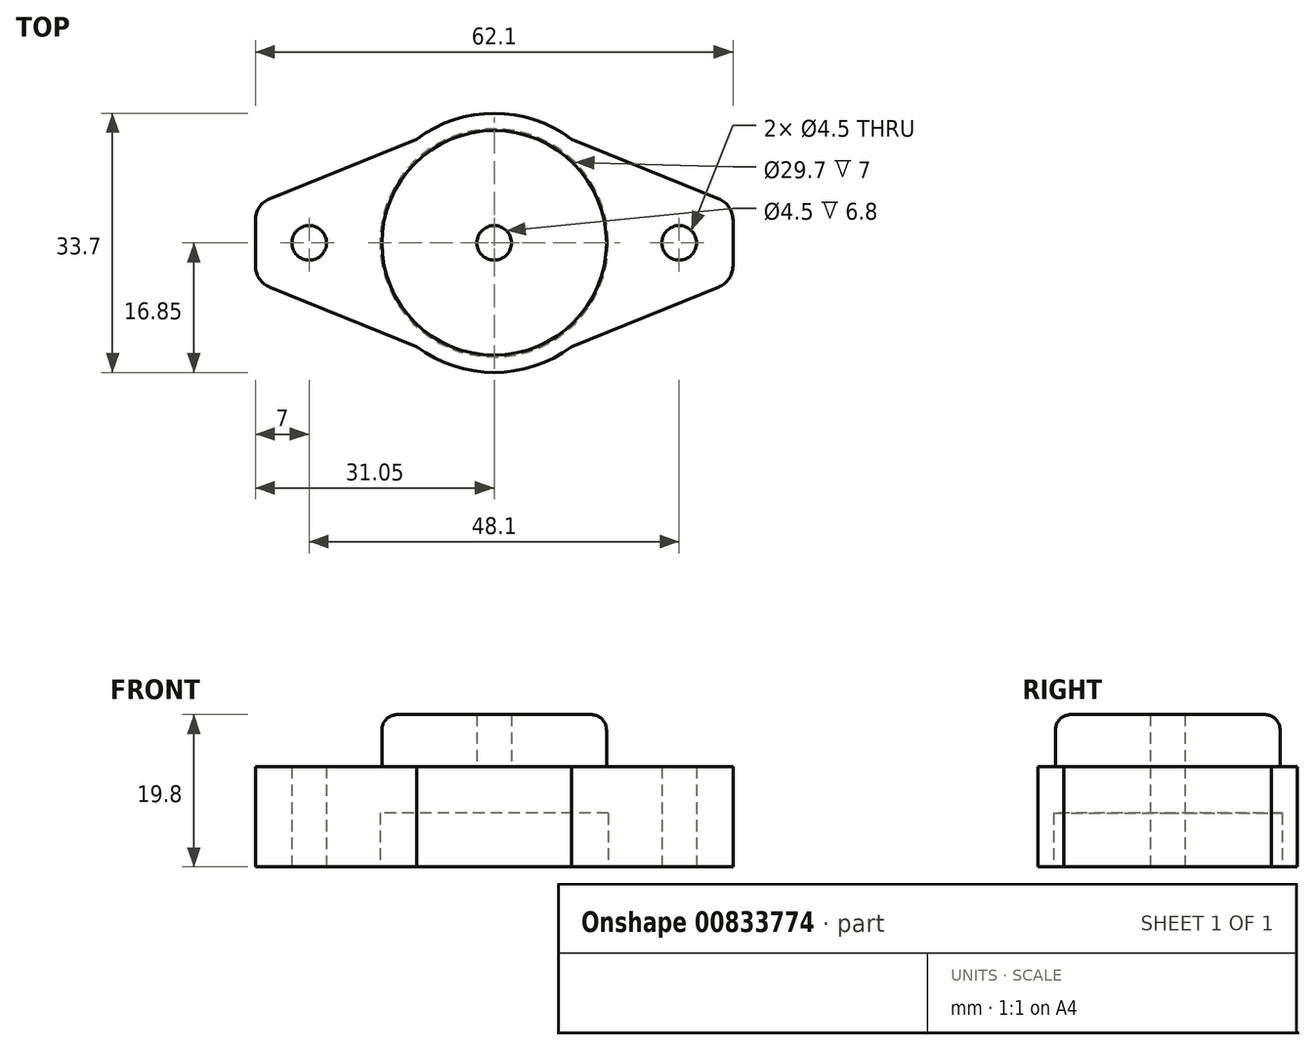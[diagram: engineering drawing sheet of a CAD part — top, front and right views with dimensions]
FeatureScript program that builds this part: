
annotation { "Feature Type Name" : "Feature", "Feature Type Description" : "" }
export const myFeature = defineFeature(function(context is Context, id is Id, definition is map)
    precondition{}
    {
        {
            var Q0;
            Q0=qCreatedBy(makeId("Top.planeOp"),FACE);
            var sketch = newSketch(context, id + "F0", { "sketchPlane" : qUnion([Q0])});
            skCircle(sketch, "E0", {"center": v(0, 0) * mm, "radius": 14.85 * mm});
            skCircle(sketch, "E1.0", {"center": v(0, 0) * mm, "radius": 16.85 * mm});
            skPoint(sketch, "E2.startSnap0", {"position": v(10.08, 0) * mm});
            skLineSegment(sketch, "E3", {"start": v(31.05, 0) * mm, "end": v(31.05, -2.98) * mm});
            skLineSegment(sketch, "E4", {"start": v(31.05, 0) * mm, "end": v(31.05, 2.98) * mm});
            skLineSegment(sketch, "E5", {"start": v(10.08, 13.5) * mm, "end": v(29.18, 5.76) * mm});
            skLineSegment(sketch, "E6", {"start": v(29.18, -5.76) * mm, "end": v(10.08, -13.5) * mm});
            skPoint(sketch, "E2.start.orphan", {"position": v(14.85, 0) * mm});
            skPoint(sketch, "E7.visualSharp", {"position": v(31.05, 5) * mm});
            skArc(sketch, "E7.filletArc", {"start": v(31.05, 2.98) * mm, "mid": v(30.54, 4.66) * mm, "end": v(29.18, 5.76) * mm});
            skPoint(sketch, "E8.visualSharp", {"position": v(31.05, -5) * mm});
            skArc(sketch, "E8.filletArc", {"start": v(29.18, -5.76) * mm, "mid": v(30.54, -4.66) * mm, "end": v(31.05, -2.98) * mm});
            skCircle(sketch, "E9", {"center": v(24.05, 0) * mm, "radius": 2.25 * mm});
            skLineSegment(sketch, "E10.MirrorCS", {"start": v(-31.05, 0) * mm, "end": v(-31.05, -2.98) * mm});
            skLineSegment(sketch, "E11.MirrorCS", {"start": v(-31.05, 0) * mm, "end": v(-31.05, 2.98) * mm});
            skArc(sketch, "E12.MirrorCS", {"start": v(-31.05, 2.98) * mm, "mid": v(-30.54, 4.66) * mm, "end": v(-29.18, 5.76) * mm});
            skArc(sketch, "E13.MirrorCS", {"start": v(-29.18, -5.76) * mm, "mid": v(-30.54, -4.66) * mm, "end": v(-31.05, -2.98) * mm});
            skCircle(sketch, "E14.MirrorC", {"center": v(-24.05, 0) * mm, "radius": 2.25 * mm});
            skPoint(sketch, "E15.MirrorP", {"position": v(-31.05, -5) * mm});
            skPoint(sketch, "E16.MirrorP", {"position": v(-31.05, 5) * mm});
            skLineSegment(sketch, "E17.MirrorCS", {"start": v(-29.18, -5.76) * mm, "end": v(-10.08, -13.5) * mm});
            skLineSegment(sketch, "E18.MirrorCS", {"start": v(-10.08, 13.5) * mm, "end": v(-29.18, 5.76) * mm});
            skPoint(sketch, "E19.MirrorP", {"position": v(-10.08, 0) * mm});
            skPoint(sketch, "E20.MirrorP", {"position": v(-14.85, 0) * mm});
            skSolve(sketch);
        }
        {
            var Q0;
            Q0 = qSketchRegion(id + "F0", true);
            extrude(context, id + "F1", {"entities" : qUnion([Q0]), "depth" : 13 * mm, "offsetDistance" : 25 * mm});
        }
        {
            var Q0;
            Q0=makeQuery(id+"F1.opExtrude","CAP_FACE",FACE,{"disambiguationData":[OSD([sQuery(id+"F0.wireOp",EDGE,"E0"),sQuery(id+"F0.wireOp",EDGE,"E1.0"),sQuery(id+"F0.wireOp",EDGE,"E3"),sQuery(id+"F0.wireOp",EDGE,"E4"),sQuery(id+"F0.wireOp",EDGE,"E5"),sQuery(id+"F0.wireOp",EDGE,"E6"),sQuery(id+"F0.wireOp",EDGE,"E7.filletArc"),sQuery(id+"F0.wireOp",EDGE,"E8.filletArc"),sQuery(id+"F0.wireOp",EDGE,"E9"),sQuery(id+"F0.wireOp",EDGE,"E10.MirrorCS"),sQuery(id+"F0.wireOp",EDGE,"E11.MirrorCS"),sQuery(id+"F0.wireOp",EDGE,"E12.MirrorCS"),sQuery(id+"F0.wireOp",EDGE,"E13.MirrorCS"),sQuery(id+"F0.wireOp",EDGE,"E14.MirrorC"),sQuery(id+"F0.wireOp",EDGE,"E17.MirrorCS"),sQuery(id+"F0.wireOp",EDGE,"E18.MirrorCS")])],"isStart":false});
            var sketch = newSketch(context, id + "F2", { "sketchPlane" : qUnion([Q0])});
            skCircle(sketch, "E21", {"center": v(0, 0) * mm, "radius": 15.05 * mm});
            skSolve(sketch);
        }
        {
            var Q0;
            Q0 = qSketchRegion(id + "F2", true);
            extrude(context, id + "F3", {"entities" : qUnion([Q0]), "operationType" : NewBodyOperationType.ADD, "oppositeDirection" : true, "depth" : 6 * mm, "offsetDistance" : 25 * mm});
        }
        {
            var Q0;
            Q0=makeQuery(id+"F3.boolean.opBoolean","MERGE",FACE,{"derivedFrom":[makeQuery(id+"F1.opExtrude","CAP_FACE",FACE,{"disambiguationData":[OSD([sQuery(id+"F0.wireOp",EDGE,"E0"),sQuery(id+"F0.wireOp",EDGE,"E1.0"),sQuery(id+"F0.wireOp",EDGE,"E3"),sQuery(id+"F0.wireOp",EDGE,"E4"),sQuery(id+"F0.wireOp",EDGE,"E5"),sQuery(id+"F0.wireOp",EDGE,"E6"),sQuery(id+"F0.wireOp",EDGE,"E7.filletArc"),sQuery(id+"F0.wireOp",EDGE,"E8.filletArc"),sQuery(id+"F0.wireOp",EDGE,"E9"),sQuery(id+"F0.wireOp",EDGE,"E10.MirrorCS"),sQuery(id+"F0.wireOp",EDGE,"E11.MirrorCS"),sQuery(id+"F0.wireOp",EDGE,"E12.MirrorCS"),sQuery(id+"F0.wireOp",EDGE,"E13.MirrorCS"),sQuery(id+"F0.wireOp",EDGE,"E14.MirrorC"),sQuery(id+"F0.wireOp",EDGE,"E17.MirrorCS"),sQuery(id+"F0.wireOp",EDGE,"E18.MirrorCS")])],"isStart":false}),makeQuery(id+"F3.opExtrude","CAP_FACE",FACE,{"disambiguationData":[OSD([sQuery(id+"F2.wireOp",EDGE,"E21")])],"isStart":true})]});
            var sketch = newSketch(context, id + "F4", { "sketchPlane" : qUnion([Q0])});
            skCircle(sketch, "E22", {"center": v(0, 0) * mm, "radius": 14.6 * mm});
            skCircle(sketch, "E23", {"center": v(0, 0) * mm, "radius": 2.25 * mm});
            skSolve(sketch);
        }
        {
            var Q0;
            Q0 = qSketchRegion(id + "F4", true);
            extrude(context, id + "F5", {"entities" : qUnion([Q0]), "operationType" : NewBodyOperationType.ADD, "depth" : 6.8 * mm, "offsetDistance" : 25 * mm});
        }
        {
            var Q0;
            Q0=makeQuery(id+"F5.opExtrude","CAP_EDGE",EDGE,{"disambiguationData":[OSD([sQuery(id+"F4.wireOp",EDGE,"E22")])],"isStart":false});
            fillet(context, id + "F6", {"entities" : qUnion([Q0]), "radius" : 2 * mm, "tangentPropagation" : true, "allowEdgeOverflow" : false});
        }
    });
